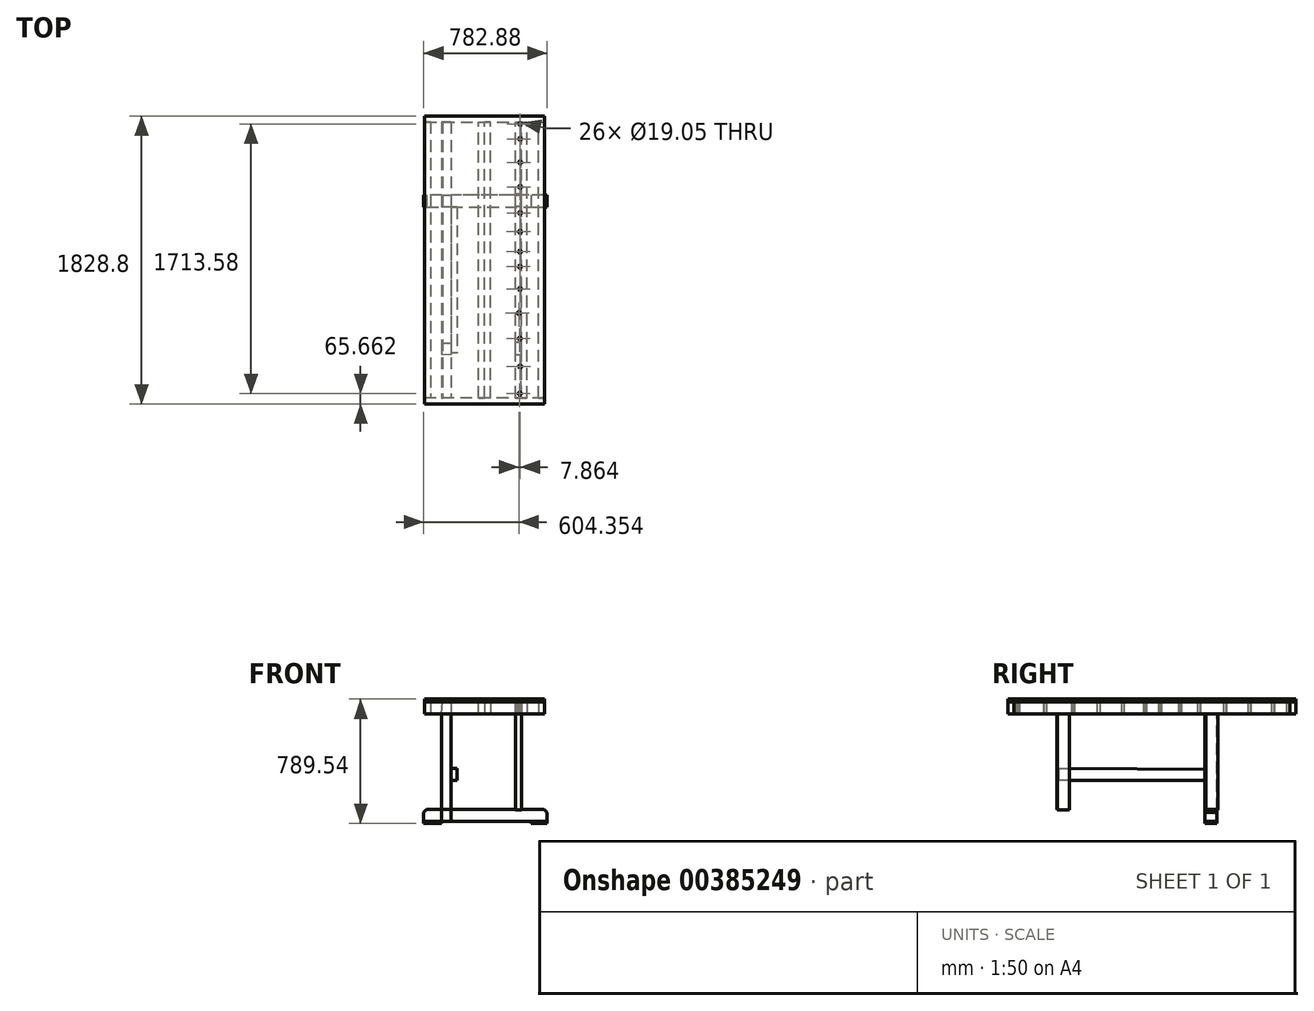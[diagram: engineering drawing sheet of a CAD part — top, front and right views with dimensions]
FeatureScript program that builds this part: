
annotation { "Feature Type Name" : "Feature", "Feature Type Description" : "" }
export const myFeature = defineFeature(function(context is Context, id is Id, definition is map)
    precondition{}
    {
        {
            var Q0;
            Q0=qCreatedBy(makeId("Top.planeOp"),FACE);
            var sketch = newSketch(context, id + "F0", { "sketchPlane" : qUnion([Q0])});
            skLineSegment(sketch, "E0", {"start": v(-224.32, -967.37) * mm, "end": v(-224.32, 861.43) * mm});
            skLineSegment(sketch, "E1", {"start": v(-224.32, 861.43) * mm, "end": v(537.68, 861.43) * mm});
            skLineSegment(sketch, "E2", {"start": v(537.68, 861.43) * mm, "end": v(537.68, -967.37) * mm});
            skLineSegment(sketch, "E3", {"start": v(537.68, -967.37) * mm, "end": v(-224.32, -967.37) * mm});
            skSolve(sketch);
        }
        {
            var Q0;
            Q0=makeQuery(id+"F0.imprint","IMPRINT",FACE,{"disambiguationData":[TD([[makeQuery(id+"F0.imprint","IMPRINT",EDGE,{"derivedFrom":sQuery(id+"F0.wireOp",EDGE,"E0")}),-1.0]])]});
            extrude(context, id + "F1", {"entities" : qUnion([Q0]), "depth" : 19.05 * mm});
        }
        {
            var Q0;
            Q0=makeQuery(id+"F1.opExtrude","CAP_FACE",FACE,{"disambiguationData":[OSD([sQuery(id+"F0.wireOp",EDGE,"E0"),sQuery(id+"F0.wireOp",EDGE,"E1"),sQuery(id+"F0.wireOp",EDGE,"E2"),sQuery(id+"F0.wireOp",EDGE,"E3")])],"isStart":true});
            var sketch = newSketch(context, id + "F2", { "sketchPlane" : qUnion([Q0])});
            skLineSegment(sketch, "E4", {"start": v(537.68, 967.37) * mm, "end": v(537.68, 929.27) * mm});
            skLineSegment(sketch, "E5", {"start": v(537.68, 929.27) * mm, "end": v(-224.32, 929.27) * mm});
            skLineSegment(sketch, "E6", {"start": v(-224.32, 929.27) * mm, "end": v(-224.32, 967.37) * mm});
            skLineSegment(sketch, "E7", {"start": v(-224.32, 967.37) * mm, "end": v(537.68, 967.37) * mm});
            skSolve(sketch);
        }
        {
            var Q0;
            Q0=makeQuery(id+"F2.imprint","IMPRINT",FACE,{"disambiguationData":[TD([[makeQuery(id+"F2.imprint","IMPRINT",EDGE,{"derivedFrom":sQuery(id+"F2.wireOp",EDGE,"E4")}),1.0]])]});
            extrude(context, id + "F3", {"entities" : qUnion([Q0]), "depth" : 76.2 * mm});
        }
        {
            var Q0;
            Q0=makeQuery(id+"F1.opExtrude","CAP_FACE",FACE,{"disambiguationData":[OSD([sQuery(id+"F0.wireOp",EDGE,"E0"),sQuery(id+"F0.wireOp",EDGE,"E1"),sQuery(id+"F0.wireOp",EDGE,"E2"),sQuery(id+"F0.wireOp",EDGE,"E3")])],"isStart":true});
            var sketch = newSketch(context, id + "F4", { "sketchPlane" : qUnion([Q0])});
            skLineSegment(sketch, "E8", {"start": v(537.68, -861.43) * mm, "end": v(-224.32, -861.43) * mm});
            skLineSegment(sketch, "E9", {"start": v(-224.32, -861.43) * mm, "end": v(-224.32, -823.33) * mm});
            skLineSegment(sketch, "E10", {"start": v(-224.32, -823.33) * mm, "end": v(537.68, -823.33) * mm});
            skLineSegment(sketch, "E11", {"start": v(537.68, -823.33) * mm, "end": v(537.68, -861.43) * mm});
            skSolve(sketch);
        }
        {
            var Q0;
            Q0=makeQuery(id+"F4.imprint","IMPRINT",FACE,{"disambiguationData":[TD([[makeQuery(id+"F4.imprint","IMPRINT",EDGE,{"derivedFrom":sQuery(id+"F4.wireOp",EDGE,"E8")}),1.0]])]});
            extrude(context, id + "F5", {"entities" : qUnion([Q0]), "depth" : 76.2 * mm});
        }
        {
            var Q0;
            Q0=makeQuery(id+"F3.opExtrude","SWEPT_FACE",FACE,{"disambiguationData":[OSD([sQuery(id+"F2.wireOp",EDGE,"E5")])]});
            var sketch = newSketch(context, id + "F6", { "sketchPlane" : qUnion([Q0])});
            skLineSegment(sketch, "E12", {"start": v(224.32, 0) * mm, "end": v(186.22, 0) * mm});
            skLineSegment(sketch, "E13", {"start": v(186.22, 0) * mm, "end": v(186.22, -76.2) * mm});
            skLineSegment(sketch, "E14", {"start": v(186.22, -76.2) * mm, "end": v(224.32, -76.2) * mm});
            skLineSegment(sketch, "E15", {"start": v(224.32, -76.2) * mm, "end": v(224.32, 0) * mm});
            skSolve(sketch);
        }
        {
            var Q0;
            Q0=makeQuery(id+"F6.imprint","IMPRINT",FACE,{"disambiguationData":[TD([[makeQuery(id+"F6.imprint","IMPRINT",EDGE,{"derivedFrom":sQuery(id+"F6.wireOp",EDGE,"E12")}),-1.0]])]});
            var sketch = newSketch(context, id + "F7", { "sketchPlane" : qUnion([Q0])});
            skSolve(sketch);
        }
        {
            var Q0;
            Q0=makeQuery(id+"F7.imprint","IMPRINT",FACE,{"disambiguationData":[TD([[makeQuery(id+"F7.imprint","IMPRINT",EDGE,{"derivedFrom":makeQuery(id+"F6.imprint","IMPRINT",EDGE,{"derivedFrom":sQuery(id+"F6.wireOp",EDGE,"E12")})}),-1.0]])]});
            extrude(context, id + "F8", {"entities" : qUnion([Q0]), "depth" : 1752.6 * mm});
        }
        {
            var Q0;
            Q0=makeQuery(id+"F5.opExtrude","SWEPT_FACE",FACE,{"disambiguationData":[OSD([sQuery(id+"F4.wireOp",EDGE,"E10")])]});
            var sketch = newSketch(context, id + "F9", { "sketchPlane" : qUnion([Q0])});
            skLineSegment(sketch, "E16", {"start": v(537.68, 0) * mm, "end": v(499.58, 0) * mm});
            skLineSegment(sketch, "E17", {"start": v(499.58, 0) * mm, "end": v(499.58, -76.2) * mm});
            skLineSegment(sketch, "E18", {"start": v(499.58, -76.2) * mm, "end": v(537.68, -76.2) * mm});
            skLineSegment(sketch, "E19", {"start": v(537.68, -76.2) * mm, "end": v(537.68, 0) * mm});
            skSolve(sketch);
        }
        {
            var Q0;
            Q0=makeQuery(id+"F9.imprint","IMPRINT",FACE,{"disambiguationData":[TD([[makeQuery(id+"F9.imprint","IMPRINT",EDGE,{"derivedFrom":sQuery(id+"F9.wireOp",EDGE,"E16")}),-1.0]])]});
            extrude(context, id + "F10", {"entities" : qUnion([Q0]), "depth" : 1752.6 * mm});
        }
        {
            var Q0;
            {var subQ0=sQuery(id+"F6.wireOp",EDGE,"E13");Q0=makeQuery(id+"F6.imprint","IMPRINT",FACE,{"disambiguationData":[TD([[makeQuery(id+"F6.imprint","IMPRINT",EDGE,{"derivedFrom":subQ0}),-1.0]])]});}
            var sketch = newSketch(context, id + "F11", { "sketchPlane" : qUnion([Q0])});
            skLineSegment(sketch, "E20", {"start": v(109.27, 0) * mm, "end": v(56.68, 0) * mm});
            skLineSegment(sketch, "E21", {"start": v(56.68, 0) * mm, "end": v(56.68, -71.99) * mm});
            skLineSegment(sketch, "E22", {"start": v(56.68, -71.99) * mm, "end": v(115.43, -71.99) * mm});
            skLineSegment(sketch, "E23", {"start": v(115.43, -71.99) * mm, "end": v(109.27, 0) * mm});
            skSolve(sketch);
        }
        {
            var Q0;
            Q0=makeQuery(id+"F11.imprint","IMPRINT",FACE,{"disambiguationData":[TD([[makeQuery(id+"F11.imprint","IMPRINT",EDGE,{"derivedFrom":sQuery(id+"F11.wireOp",EDGE,"E20")}),-1.0]])]});
            extrude(context, id + "F12", {"entities" : qUnion([Q0]), "depth" : 1752.6 * mm});
        }
        {
            var Q0;
            Q0=makeQuery(id+"F5.opExtrude","SWEPT_FACE",FACE,{"disambiguationData":[OSD([sQuery(id+"F4.wireOp",EDGE,"E10")])]});
            var sketch = newSketch(context, id + "F13", { "sketchPlane" : qUnion([Q0])});
            skLineSegment(sketch, "E24", {"start": v(156.68, 0) * mm, "end": v(156.68, -76.2) * mm});
            skLineSegment(sketch, "E25", {"start": v(156.68, -76.2) * mm, "end": v(118.58, -76.2) * mm});
            skLineSegment(sketch, "E26", {"start": v(118.58, -76.2) * mm, "end": v(118.58, 0) * mm});
            skLineSegment(sketch, "E27", {"start": v(118.58, 0) * mm, "end": v(156.68, 0) * mm});
            skSolve(sketch);
        }
        {
            var Q0;
            Q0=makeQuery(id+"F13.imprint","IMPRINT",FACE,{"disambiguationData":[TD([[makeQuery(id+"F13.imprint","IMPRINT",EDGE,{"derivedFrom":sQuery(id+"F13.wireOp",EDGE,"E24")}),-1.0]])]});
            extrude(context, id + "F14", {"entities" : qUnion([Q0]), "depth" : 1752.6 * mm});
        }
        {
            var Q0;
            Q0=makeQuery(id+"F5.opExtrude","SWEPT_FACE",FACE,{"disambiguationData":[OSD([sQuery(id+"F4.wireOp",EDGE,"E10")])]});
            var sketch = newSketch(context, id + "F15", { "sketchPlane" : qUnion([Q0])});
            skLineSegment(sketch, "E28", {"start": v(425.67, 0) * mm, "end": v(425.67, -76.2) * mm});
            skLineSegment(sketch, "E29", {"start": v(425.67, -76.2) * mm, "end": v(387.57, -76.2) * mm});
            skLineSegment(sketch, "E30", {"start": v(387.57, -76.2) * mm, "end": v(387.57, 0) * mm});
            skLineSegment(sketch, "E31", {"start": v(387.57, 0) * mm, "end": v(425.67, 0) * mm});
            skSolve(sketch);
        }
        {
            var Q0;
            Q0=makeQuery(id+"F15.imprint","IMPRINT",FACE,{"disambiguationData":[TD([[makeQuery(id+"F15.imprint","IMPRINT",EDGE,{"derivedFrom":sQuery(id+"F15.wireOp",EDGE,"E28")}),-1.0]])]});
            extrude(context, id + "F16", {"entities" : qUnion([Q0]), "depth" : 1752.6 * mm});
        }
        {
            var Q0;
            Q0=makeQuery(id+"F5.opExtrude","SWEPT_FACE",FACE,{"disambiguationData":[OSD([sQuery(id+"F4.wireOp",EDGE,"E10")])]});
            var sketch = newSketch(context, id + "F17", { "sketchPlane" : qUnion([Q0])});
            skLineSegment(sketch, "E32", {"start": v(392.76, 0) * mm, "end": v(392.76, -76.2) * mm});
            skLineSegment(sketch, "E33", {"start": v(392.76, -76.2) * mm, "end": v(354.66, -76.2) * mm});
            skLineSegment(sketch, "E34", {"start": v(354.66, -76.2) * mm, "end": v(354.66, 0) * mm});
            skLineSegment(sketch, "E35", {"start": v(354.66, 0) * mm, "end": v(392.76, 0) * mm});
            skSolve(sketch);
        }
        {
            var Q0;
            Q0=makeQuery(id+"F17.imprint","IMPRINT",FACE,{"disambiguationData":[TD([[makeQuery(id+"F17.imprint","IMPRINT",EDGE,{"derivedFrom":sQuery(id+"F17.wireOp",EDGE,"E32")}),-1.0]])]});
            var sketch = newSketch(context, id + "F18", { "sketchPlane" : qUnion([Q0])});
            skSolve(sketch);
        }
        {
            var Q0;
            Q0=makeQuery(id+"F18.imprint","IMPRINT",FACE,{"disambiguationData":[TD([[makeQuery(id+"F18.imprint","IMPRINT",EDGE,{"derivedFrom":makeQuery(id+"F17.imprint","IMPRINT",EDGE,{"derivedFrom":sQuery(id+"F17.wireOp",EDGE,"E32")})}),-1.0]])]});
            extrude(context, id + "F19", {"entities" : qUnion([Q0]), "depth" : 1752.6 * mm});
        }
        {
            var Q0;
            Q0=makeQuery(id+"F1.opExtrude","CAP_FACE",FACE,{"disambiguationData":[OSD([sQuery(id+"F0.wireOp",EDGE,"E0"),sQuery(id+"F0.wireOp",EDGE,"E1"),sQuery(id+"F0.wireOp",EDGE,"E2"),sQuery(id+"F0.wireOp",EDGE,"E3")])],"isStart":false});
            var sketch = newSketch(context, id + "F20", { "sketchPlane" : qUnion([Q0])});
            skLineSegment(sketch, "E36", {"start": v(382.42, 861.43) * mm, "end": v(382.42, -967.37) * mm});
            skSolve(sketch);
        }
        {
            var Q0;
            {var subQ0=sQuery(id+"F20.wireOp",EDGE,"E36");Q0=makeQuery(id+"F20.imprint","IMPRINT",FACE,{"disambiguationData":[TD([[makeQuery(id+"F20.imprint","IMPRINT",EDGE,{"derivedFrom":subQ0}),-1.0]])]});}
            var sketch = newSketch(context, id + "F21", { "sketchPlane" : qUnion([Q0])});
            skPoint(sketch, "E37", {"position": v(379.94, -901.7) * mm});
            skPoint(sketch, "E38", {"position": v(382.22, -729.34) * mm});
            skPoint(sketch, "E39", {"position": v(379.78, -552.13) * mm});
            skPoint(sketch, "E40", {"position": v(374.88, -390.01) * mm});
            skPoint(sketch, "E41", {"position": v(381.42, -236.7) * mm});
            skPoint(sketch, "E42", {"position": v(381.42, -95.25) * mm});
            skPoint(sketch, "E43", {"position": v(381.42, 0) * mm});
            skPoint(sketch, "E44", {"position": v(381.73, 127.09) * mm});
            skPoint(sketch, "E45", {"position": v(382.75, 246.43) * mm});
            skPoint(sketch, "E46", {"position": v(382.75, 411.42) * mm});
            skPoint(sketch, "E47", {"position": v(382.75, 567.06) * mm});
            skPoint(sketch, "E48", {"position": v(382.75, 716.43) * mm});
            skPoint(sketch, "E49", {"position": v(382.75, 811.87) * mm});
            skSolve(sketch);
        }
        {
            var Q0;
            Q0=sQuery(id+"F21.wireOp",VERTEX,"E44");
            var Q1;
            Q1=sQuery(id+"F21.wireOp",VERTEX,"E37");
            var Q2;
            Q2=sQuery(id+"F21.wireOp",VERTEX,"E45");
            var Q3;
            Q3=sQuery(id+"F21.wireOp",VERTEX,"E48");
            var Q4;
            Q4=sQuery(id+"F21.wireOp",VERTEX,"E47");
            var Q5;
            Q5=sQuery(id+"F21.wireOp",VERTEX,"E42");
            var Q6;
            Q6=sQuery(id+"F21.wireOp",VERTEX,"E40");
            var Q7;
            Q7=sQuery(id+"F21.wireOp",VERTEX,"E39");
            var Q8;
            Q8=sQuery(id+"F21.wireOp",VERTEX,"E38");
            var Q9;
            Q9=sQuery(id+"F21.wireOp",VERTEX,"E49");
            var Q10;
            Q10=sQuery(id+"F21.wireOp",VERTEX,"E43");
            var Q11;
            Q11=sQuery(id+"F21.wireOp",VERTEX,"E41");
            var Q12;
            Q12=sQuery(id+"F21.wireOp",VERTEX,"E46");
            var Q13;
            Q13=makeQuery(id+"F1.opExtrude","SWEPT_BODY",BODY,{"disambiguationData":[OSD([sQuery(id+"F0.wireOp",EDGE,"E0"),sQuery(id+"F0.wireOp",EDGE,"E1"),sQuery(id+"F0.wireOp",EDGE,"E2"),sQuery(id+"F0.wireOp",EDGE,"E3")])]});
            var Q14;
            Q14=makeQuery(id+"F16.opExtrude","SWEPT_BODY",BODY,{"disambiguationData":[OSD([sQuery(id+"F15.wireOp",EDGE,"E28"),sQuery(id+"F15.wireOp",EDGE,"E29"),sQuery(id+"F15.wireOp",EDGE,"E30"),sQuery(id+"F15.wireOp",EDGE,"E31")])]});
            var Q15;
            Q15=makeQuery(id+"F19.opExtrude","SWEPT_BODY",BODY,{"disambiguationData":[OSD([sQuery(id+"F17.wireOp",EDGE,"E32"),sQuery(id+"F17.wireOp",EDGE,"E33"),sQuery(id+"F17.wireOp",EDGE,"E34"),sQuery(id+"F17.wireOp",EDGE,"E35")])]});
            hole(context, id + "F22", {"style" : HoleStyle.SIMPLE, "endStyle" : HoleEndStyle.THROUGH, "holeDiameter" : 19.05 * mm, "isTappedThrough" : true, "tappedDepth" : 12.7 * mm, "tapClearance" : 3, "locations" : qUnion([Q0, Q1, Q2, Q3, Q4, Q5, Q6, Q7, Q8, Q9, Q10, Q11, Q12]), "scope" : qUnion([Q13, Q14, Q15])});
        }
        {
            var Q0;
            Q0=makeQuery(id+"F12.opExtrude","SWEPT_FACE",FACE,{"disambiguationData":[OSD([sQuery(id+"F11.wireOp",EDGE,"E22")])]});
            var sketch = newSketch(context, id + "F23", { "sketchPlane" : qUnion([Q0])});
            skLineSegment(sketch, "E50", {"start": v(-115.43, 654.62) * mm, "end": v(-115.43, 579.84) * mm});
            skLineSegment(sketch, "E51", {"start": v(-115.43, 579.84) * mm, "end": v(-56.68, 579.84) * mm});
            skLineSegment(sketch, "E52", {"start": v(-56.68, 579.84) * mm, "end": v(-56.68, 656.04) * mm});
            skLineSegment(sketch, "E53", {"start": v(-56.68, 656.04) * mm, "end": v(-115.43, 654.62) * mm});
            skSolve(sketch);
        }
        {
            var Q0;
            Q0=makeQuery(id+"F23.imprint","IMPRINT",FACE,{"disambiguationData":[TD([[makeQuery(id+"F23.imprint","IMPRINT",EDGE,{"derivedFrom":sQuery(id+"F23.wireOp",EDGE,"E50")}),-1.0]])]});
            extrude(context, id + "F24", {"entities" : qUnion([Q0]), "depth" : 609.6 * mm});
        }
        {
            var Q0;
            Q0=makeQuery(id+"F12.opExtrude","SWEPT_FACE",FACE,{"disambiguationData":[OSD([sQuery(id+"F11.wireOp",EDGE,"E22")])]});
            var sketch = newSketch(context, id + "F25", { "sketchPlane" : qUnion([Q0])});
            skLineSegment(sketch, "E54", {"start": v(-115.43, -358.45) * mm, "end": v(-56.68, -358.45) * mm});
            skLineSegment(sketch, "E55", {"start": v(-56.68, -358.45) * mm, "end": v(-56.68, -282.25) * mm});
            skLineSegment(sketch, "E56", {"start": v(-56.68, -282.25) * mm, "end": v(-115.43, -282.25) * mm});
            skLineSegment(sketch, "E57", {"start": v(-115.43, -282.25) * mm, "end": v(-115.43, -358.45) * mm});
            skSolve(sketch);
        }
        {
            var Q0;
            Q0=makeQuery(id+"F25.imprint","IMPRINT",FACE,{"disambiguationData":[TD([[makeQuery(id+"F25.imprint","IMPRINT",EDGE,{"derivedFrom":sQuery(id+"F25.wireOp",EDGE,"E54")}),1.0]])]});
            extrude(context, id + "F26", {"entities" : qUnion([Q0]), "depth" : 609.6 * mm});
        }
        {
            var Q0;
            Q0=makeQuery(id+"F19.opExtrude","SWEPT_FACE",FACE,{"disambiguationData":[OSD([sQuery(id+"F17.wireOp",EDGE,"E33")])]});
            var sketch = newSketch(context, id + "F27", { "sketchPlane" : qUnion([Q0])});
            skLineSegment(sketch, "E58", {"start": v(354.66, 577.37) * mm, "end": v(354.66, 653.57) * mm});
            skLineSegment(sketch, "E59", {"start": v(354.66, 653.57) * mm, "end": v(392.76, 653.57) * mm});
            skLineSegment(sketch, "E60", {"start": v(392.76, 653.57) * mm, "end": v(392.76, 576.83) * mm});
            skLineSegment(sketch, "E61", {"start": v(392.76, 576.83) * mm, "end": v(354.66, 577.37) * mm});
            skSolve(sketch);
        }
        {
            var Q0;
            Q0=makeQuery(id+"F27.imprint","IMPRINT",FACE,{"disambiguationData":[TD([[makeQuery(id+"F27.imprint","IMPRINT",EDGE,{"derivedFrom":sQuery(id+"F27.wireOp",EDGE,"E58")}),1.0]])]});
            extrude(context, id + "F28", {"entities" : qUnion([Q0]), "depth" : 609.6 * mm});
        }
        {
            var Q0;
            Q0=makeQuery(id+"F19.opExtrude","SWEPT_FACE",FACE,{"disambiguationData":[OSD([sQuery(id+"F17.wireOp",EDGE,"E33")])]});
            var sketch = newSketch(context, id + "F29", { "sketchPlane" : qUnion([Q0])});
            skLineSegment(sketch, "E62", {"start": v(354.66, -364.33) * mm, "end": v(354.66, -288.13) * mm});
            skLineSegment(sketch, "E63", {"start": v(354.66, -288.13) * mm, "end": v(392.76, -288.13) * mm});
            skLineSegment(sketch, "E64", {"start": v(392.76, -288.13) * mm, "end": v(392.76, -364.33) * mm});
            skLineSegment(sketch, "E65", {"start": v(392.76, -364.33) * mm, "end": v(354.66, -364.33) * mm});
            skSolve(sketch);
        }
        {
            var Q0;
            Q0=makeQuery(id+"F29.imprint","IMPRINT",FACE,{"disambiguationData":[TD([[makeQuery(id+"F29.imprint","IMPRINT",EDGE,{"derivedFrom":sQuery(id+"F29.wireOp",EDGE,"E62")}),1.0]])]});
            extrude(context, id + "F30", {"entities" : qUnion([Q0]), "depth" : 609.6 * mm});
        }
        {
            var Q0;
            Q0=makeQuery(id+"F26.opExtrude","CAP_FACE",FACE,{"disambiguationData":[OSD([sQuery(id+"F25.wireOp",EDGE,"E54"),sQuery(id+"F25.wireOp",EDGE,"E55"),sQuery(id+"F25.wireOp",EDGE,"E56"),sQuery(id+"F25.wireOp",EDGE,"E57")])],"isStart":false});
            var sketch = newSketch(context, id + "F31", { "sketchPlane" : qUnion([Q0])});
            skLineSegment(sketch, "E66", {"start": v(-229.47, -358.45) * mm, "end": v(-229.47, -282.25) * mm});
            skLineSegment(sketch, "E67", {"start": v(-229.47, -282.25) * mm, "end": v(553.4, -282.25) * mm});
            skLineSegment(sketch, "E68", {"start": v(553.4, -282.25) * mm, "end": v(553.4, -358.45) * mm});
            skLineSegment(sketch, "E69", {"start": v(553.4, -358.45) * mm, "end": v(-229.47, -358.45) * mm});
            skSolve(sketch);
        }
        {
            var Q0;
            {var subQ2=sQuery(id+"F31.wireOp",EDGE,"E68");Q0=makeQuery(id+"F31.imprint","IMPRINT",FACE,{"disambiguationData":[TD([[makeQuery(id+"F31.imprint","IMPRINT",EDGE,{"derivedFrom":subQ2}),-1.0]])]});}
            var Q1;
            {var subQ0=sQuery(id+"F31.wireOp",EDGE,"E66");Q1=makeQuery(id+"F31.imprint","IMPRINT",FACE,{"disambiguationData":[TD([[makeQuery(id+"F31.imprint","IMPRINT",EDGE,{"derivedFrom":subQ0}),-1.0]])]});}
            extrude(context, id + "F32", {"entities" : qUnion([Q0, Q1]), "operationType" : NewBodyOperationType.ADD, "depth" : 76.2 * mm});
        }
        {
            var Q0;
            Q0=makeQuery(id+"F32.opExtrude","CAP_EDGE",EDGE,{"disambiguationData":[OSD([sQuery(id+"F31.wireOp",EDGE,"E68")])],"isStart":true});
            chamfer(context, id + "F33", {"entities" : qUnion([Q0]), "width" : 19.05 * mm, "tangentPropagation" : true});
        }
        {
            var Q0;
            Q0=makeQuery(id+"F32.opExtrude","CAP_EDGE",EDGE,{"disambiguationData":[OSD([sQuery(id+"F31.wireOp",EDGE,"E66")])],"isStart":true});
            chamfer(context, id + "F34", {"entities" : qUnion([Q0]), "width" : 19.05 * mm, "tangentPropagation" : true});
        }
        {
            var Q0;
            Q0=makeQuery(id+"F26.opExtrude","CAP_FACE",FACE,{"disambiguationData":[OSD([sQuery(id+"F25.wireOp",EDGE,"E54"),sQuery(id+"F25.wireOp",EDGE,"E55"),sQuery(id+"F25.wireOp",EDGE,"E56"),sQuery(id+"F25.wireOp",EDGE,"E57")])],"isStart":false});
            var sketch = newSketch(context, id + "F35", { "sketchPlane" : qUnion([Q0])});
            skLineSegment(sketch, "E70", {"start": v(-56.68, -358.45) * mm, "end": v(-115.43, -358.45) * mm});
            skLineSegment(sketch, "E71", {"start": v(-115.43, -358.45) * mm, "end": v(-115.43, -282.25) * mm});
            skLineSegment(sketch, "E72", {"start": v(-115.43, -282.25) * mm, "end": v(-56.68, -282.25) * mm});
            skLineSegment(sketch, "E73", {"start": v(-56.68, -282.25) * mm, "end": v(-56.68, -358.45) * mm});
            skSolve(sketch);
        }
        {
            var Q0;
            Q0=makeQuery(id+"F35.imprint","IMPRINT",FACE,{"disambiguationData":[TD([[makeQuery(id+"F35.imprint","IMPRINT",EDGE,{"derivedFrom":sQuery(id+"F35.wireOp",EDGE,"E70")}),1.0]])]});
            extrude(context, id + "F36", {"entities" : qUnion([Q0]), "depth" : 76.2 * mm});
        }
        {
            var Q0;
            Q0=makeQuery(id+"F32.opExtrude","CAP_FACE",FACE,{"disambiguationData":[OSD([sQuery(id+"F25.wireOp",EDGE,"E55"),sQuery(id+"F31.wireOp",EDGE,"E67"),sQuery(id+"F31.wireOp",EDGE,"E68"),sQuery(id+"F31.wireOp",EDGE,"E69")])],"isStart":false});
            var sketch = newSketch(context, id + "F37", { "sketchPlane" : qUnion([Q0])});
            skLineSegment(sketch, "E74", {"start": v(553.4, -358.45) * mm, "end": v(451.8, -358.45) * mm});
            skLineSegment(sketch, "E75", {"start": v(451.8, -358.45) * mm, "end": v(451.8, -282.25) * mm});
            skLineSegment(sketch, "E76", {"start": v(451.8, -282.25) * mm, "end": v(553.4, -282.25) * mm});
            skLineSegment(sketch, "E77", {"start": v(553.4, -282.25) * mm, "end": v(553.4, -358.45) * mm});
            skSolve(sketch);
        }
        {
            var Q0;
            Q0=makeQuery(id+"F32.opExtrude","CAP_FACE",FACE,{"disambiguationData":[OSD([sQuery(id+"F25.wireOp",EDGE,"E57"),sQuery(id+"F31.wireOp",EDGE,"E66"),sQuery(id+"F31.wireOp",EDGE,"E67"),sQuery(id+"F31.wireOp",EDGE,"E69")])],"isStart":false});
            var sketch = newSketch(context, id + "F38", { "sketchPlane" : qUnion([Q0])});
            skLineSegment(sketch, "E78", {"start": v(-229.47, -358.45) * mm, "end": v(-229.47, -282.25) * mm});
            skLineSegment(sketch, "E79", {"start": v(-229.47, -282.25) * mm, "end": v(-115.43, -282.25) * mm});
            skLineSegment(sketch, "E80", {"start": v(-115.43, -282.25) * mm, "end": v(-115.43, -358.45) * mm});
            skLineSegment(sketch, "E81", {"start": v(-115.43, -358.45) * mm, "end": v(-229.47, -358.45) * mm});
            skSolve(sketch);
        }
        {
            var Q0;
            Q0=makeQuery(id+"F37.imprint","IMPRINT",FACE,{"disambiguationData":[TD([[makeQuery(id+"F37.imprint","IMPRINT",EDGE,{"derivedFrom":sQuery(id+"F37.wireOp",EDGE,"E74")}),-1.0]])]});
            extrude(context, id + "F39", {"entities" : qUnion([Q0]), "depth" : 12.7 * mm});
        }
        {
            var Q0;
            Q0=makeQuery(id+"F38.imprint","IMPRINT",FACE,{"disambiguationData":[TD([[makeQuery(id+"F38.imprint","IMPRINT",EDGE,{"derivedFrom":sQuery(id+"F38.wireOp",EDGE,"E78")}),-1.0]])]});
            extrude(context, id + "F40", {"entities" : qUnion([Q0]), "depth" : 12.7 * mm});
        }
        {
            var Q0;
            Q0=makeQuery(id+"F26.opExtrude","SWEPT_FACE",FACE,{"disambiguationData":[OSD([sQuery(id+"F25.wireOp",EDGE,"E55")])]});
            var sketch = newSketch(context, id + "F41", { "sketchPlane" : qUnion([Q0])});
            skLineSegment(sketch, "E82", {"start": v(358.45, -428.36) * mm, "end": v(358.45, -497.42) * mm});
            skLineSegment(sketch, "E83", {"start": v(358.45, -497.42) * mm, "end": v(-643.75, -497.42) * mm});
            skLineSegment(sketch, "E84", {"start": v(-643.75, -497.42) * mm, "end": v(-643.75, -421.22) * mm});
            skLineSegment(sketch, "E85", {"start": v(-643.75, -421.22) * mm, "end": v(358.45, -428.36) * mm});
            skSolve(sketch);
        }
        {
            var Q0;
            {var subQ0=sQuery(id+"F41.wireOp",EDGE,"E84");Q0=makeQuery(id+"F41.imprint","IMPRINT",FACE,{"disambiguationData":[TD([[makeQuery(id+"F41.imprint","IMPRINT",EDGE,{"derivedFrom":subQ0}),-1.0]])]});}
            var Q1;
            Q1=makeQuery(id+"F14.opExtrude","SWEPT_FACE",FACE,{"disambiguationData":[OSD([sQuery(id+"F13.wireOp",EDGE,"E24")])]});
            extrude(context, id + "F42", {"entities" : qUnion([Q0, Q1]), "depth" : 38.1 * mm});
        }
    });
